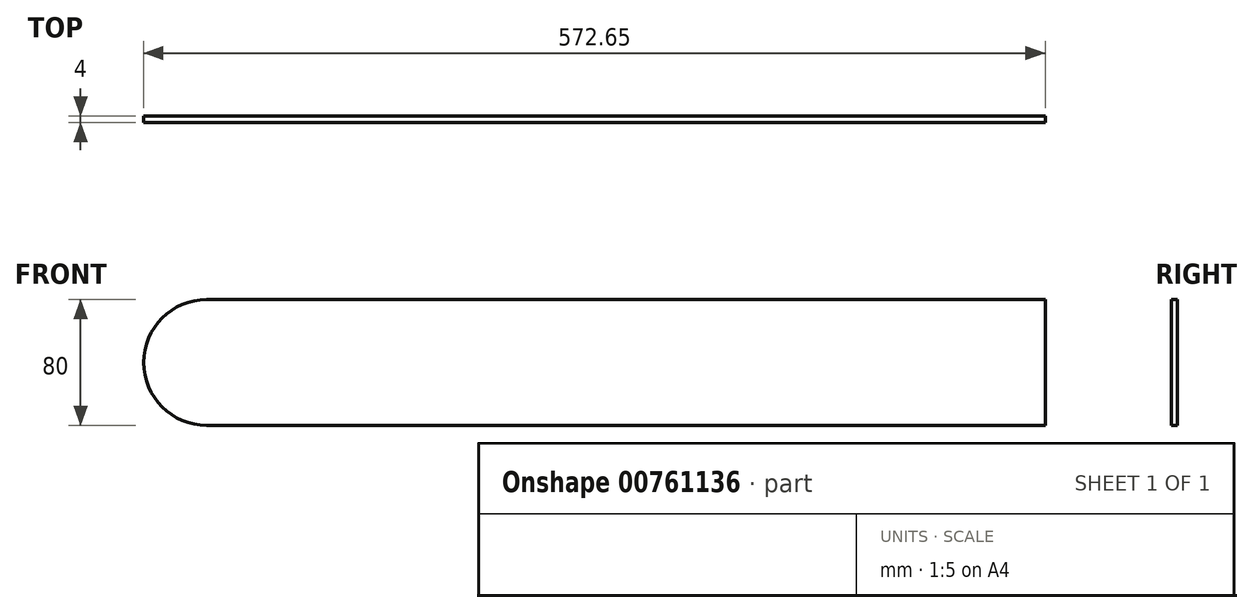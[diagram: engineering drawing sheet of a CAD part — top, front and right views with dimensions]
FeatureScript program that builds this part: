
annotation { "Feature Type Name" : "Feature", "Feature Type Description" : "" }
export const myFeature = defineFeature(function(context is Context, id is Id, definition is map)
    precondition{}
    {
        {
            var Q0;
            Q0=qCreatedBy(makeId("Front.planeOp"),FACE);
            var sketch = newSketch(context, id + "F0", { "sketchPlane" : qUnion([Q0])});
            skCircle(sketch, "E0", {"center": v(0, 0) * mm, "radius": 40 * mm, "construction": true});
            skLineSegment(sketch, "E1", {"start": v(0, 40) * mm, "end": v(532.65, 40) * mm});
            skLineSegment(sketch, "E2", {"start": v(0, -40) * mm, "end": v(532.65, -40) * mm});
            skArc(sketch, "E3", {"start": v(0, 40) * mm, "mid": v(-40, 0) * mm, "end": v(0, -40) * mm});
            skLineSegment(sketch, "E4", {"start": v(532.65, -40) * mm, "end": v(532.65, 40) * mm});
            skSolve(sketch);
        }
        {
            var Q0;
            Q0=makeQuery(id+"F0.imprint","IMPRINT",FACE,{"disambiguationData":[TD([[makeQuery(id+"F0.imprint","IMPRINT",EDGE,{"derivedFrom":sQuery(id+"F0.wireOp",EDGE,"E1")}),-1.0]])]});
            extrude(context, id + "F1", {"entities" : qUnion([Q0]), "depth" : 4 * mm, "offsetDistance" : 25 * mm});
        }
    });
